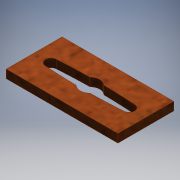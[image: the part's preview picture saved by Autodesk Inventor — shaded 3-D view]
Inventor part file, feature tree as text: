
AUTODESK INVENTOR PART (.ipt)
format: ipt  version: 2016 (Build 200138000, 138)  size: 121,344 bytes
history: native  units: mm
features: other x1, extrude x1, sketch x1
ambient origin geometry x8: Origin, YZ Plane, XZ Plane, XY Plane, X Axis, Y Axis, Z Axis, Center Point
bodies: Body1 (feature_tree)
feature tree (3):
  other  "Sólido1"
  extrude  "Extrusión1"  Depth=3.0mm TaperAngle=0.0deg
  sketch  "Boceto1"  dims[d2=40.0mm d3=3.0mm d4=0.0mm]
